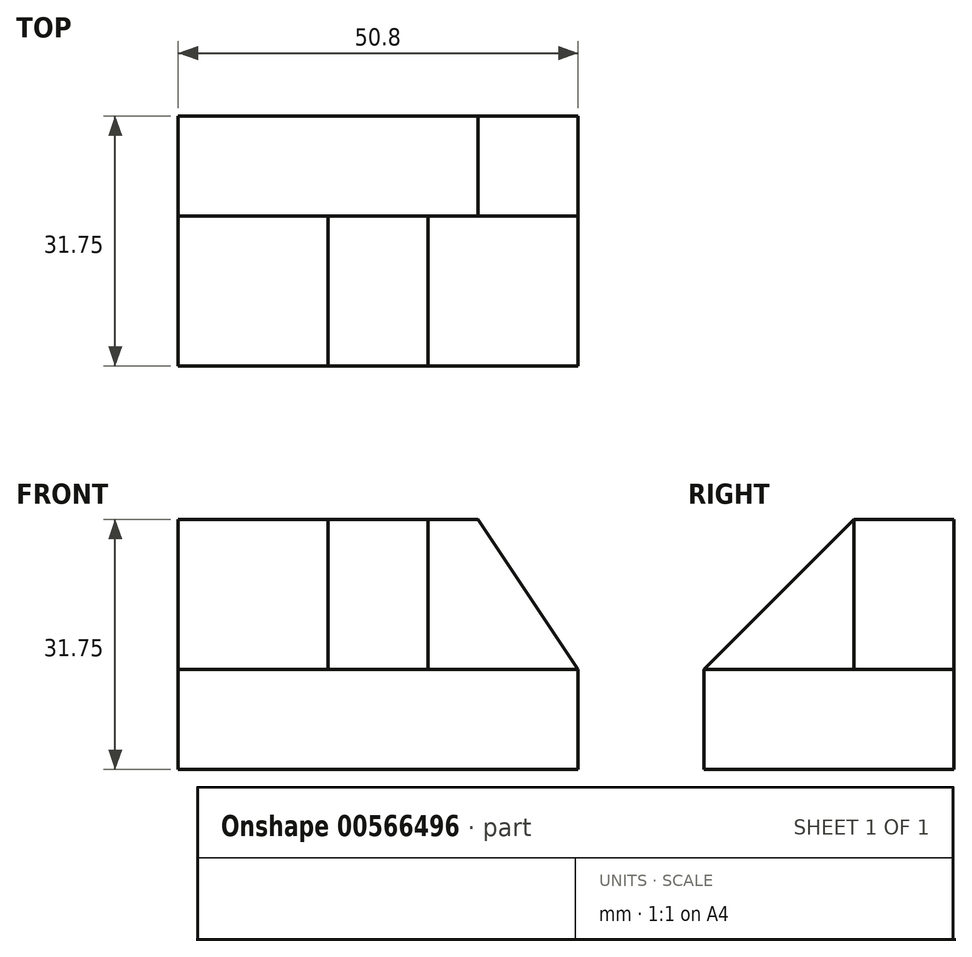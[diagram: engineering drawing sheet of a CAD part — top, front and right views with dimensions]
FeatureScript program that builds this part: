
annotation { "Feature Type Name" : "Feature", "Feature Type Description" : "" }
export const myFeature = defineFeature(function(context is Context, id is Id, definition is map)
    precondition{}
    {
        {
            var Q0;
            Q0=qCreatedBy(makeId("Right.planeOp"),FACE);
            var sketch = newSketch(context, id + "F0", { "sketchPlane" : qUnion([Q0])});
            skLineSegment(sketch, "E0", {"start": v(-19.5, 41.82) * mm, "end": v(-19.5, 10.07) * mm});
            skLineSegment(sketch, "E1", {"start": v(-19.5, 10.07) * mm, "end": v(-51.25, 10.07) * mm});
            skLineSegment(sketch, "E2", {"start": v(-51.25, 10.07) * mm, "end": v(-51.25, 22.77) * mm});
            skLineSegment(sketch, "E3", {"start": v(-51.25, 22.77) * mm, "end": v(-32.2, 22.77) * mm});
            skLineSegment(sketch, "E4", {"start": v(-32.2, 22.77) * mm, "end": v(-32.2, 41.82) * mm});
            skLineSegment(sketch, "E5", {"start": v(-32.2, 41.82) * mm, "end": v(-19.5, 41.82) * mm});
            skSolve(sketch);
        }
        {
            var Q0;
            Q0=makeQuery(id+"F0.imprint","IMPRINT",FACE,{"disambiguationData":[TD([[makeQuery(id+"F0.imprint","IMPRINT",EDGE,{"derivedFrom":sQuery(id+"F0.wireOp",EDGE,"E0")}),-1.0]])]});
            extrude(context, id + "F1", {"entities" : qUnion([Q0]), "depth" : 50.8 * mm, "offsetDistance" : 25.4 * mm});
        }
        {
            var Q0;
            Q0=makeQuery(id+"F1.opExtrude","SWEPT_FACE",FACE,{"disambiguationData":[OSD([sQuery(id+"F0.wireOp",EDGE,"E0")])]});
            var sketch = newSketch(context, id + "F2", { "sketchPlane" : qUnion([Q0])});
            skLineSegment(sketch, "E6", {"start": v(-38.1, 41.82) * mm, "end": v(-50.8, 22.77) * mm});
            skSolve(sketch);
        }
        {
            var Q0;
            {var subQ0=sQuery(id+"F2.wireOp",EDGE,"E6");Q0=makeQuery(id+"F2.imprint","IMPRINT",FACE,{"disambiguationData":[TD([[makeQuery(id+"F2.imprint","IMPRINT",EDGE,{"derivedFrom":subQ0}),-1.0]])]});}
            extrude(context, id + "F3", {"entities" : qUnion([Q0]), "operationType" : NewBodyOperationType.REMOVE, "oppositeDirection" : true, "depth" : 25.4 * mm, "offsetDistance" : 25.4 * mm});
        }
        {
            var Q0;
            Q0=makeQuery(id+"F1.opExtrude","SWEPT_FACE",FACE,{"disambiguationData":[OSD([sQuery(id+"F0.wireOp",EDGE,"E4")])]});
            var sketch = newSketch(context, id + "F4", { "sketchPlane" : qUnion([Q0])});
            skLineSegment(sketch, "E7", {"start": v(31.75, 41.82) * mm, "end": v(31.75, 22.77) * mm});
            skLineSegment(sketch, "E8", {"start": v(31.75, 22.77) * mm, "end": v(19.05, 22.77) * mm});
            skLineSegment(sketch, "E9", {"start": v(19.05, 22.77) * mm, "end": v(19.05, 41.82) * mm});
            skLineSegment(sketch, "E10", {"start": v(19.05, 41.82) * mm, "end": v(31.75, 41.82) * mm});
            skSolve(sketch);
        }
        {
            var Q0;
            Q0=makeQuery(id+"F4.imprint","IMPRINT",FACE,{"disambiguationData":[TD([[makeQuery(id+"F4.imprint","IMPRINT",EDGE,{"derivedFrom":sQuery(id+"F4.wireOp",EDGE,"E7")}),-1.0]])]});
            extrude(context, id + "F5", {"entities" : qUnion([Q0]), "operationType" : NewBodyOperationType.ADD, "depth" : 19.05 * mm, "offsetDistance" : 25.4 * mm});
        }
        {
            var Q0;
            Q0=makeQuery(id+"F5.opExtrude","SWEPT_FACE",FACE,{"disambiguationData":[OSD([sQuery(id+"F4.wireOp",EDGE,"E9")])]});
            var sketch = newSketch(context, id + "F6", { "sketchPlane" : qUnion([Q0])});
            skLineSegment(sketch, "E11", {"start": v(32.2, 41.82) * mm, "end": v(51.25, 22.77) * mm});
            skSolve(sketch);
        }
        {
            var Q0;
            Q0=makeQuery(id+"F6.imprint","IMPRINT",FACE,{"disambiguationData":[TD([[makeQuery(id+"F6.imprint","IMPRINT",EDGE,{"derivedFrom":sQuery(id+"F6.wireOp",EDGE,"E11")}),1.0]])]});
            extrude(context, id + "F7", {"entities" : qUnion([Q0]), "operationType" : NewBodyOperationType.REMOVE, "oppositeDirection" : true, "depth" : 25.4 * mm, "offsetDistance" : 25.4 * mm});
        }
    });
